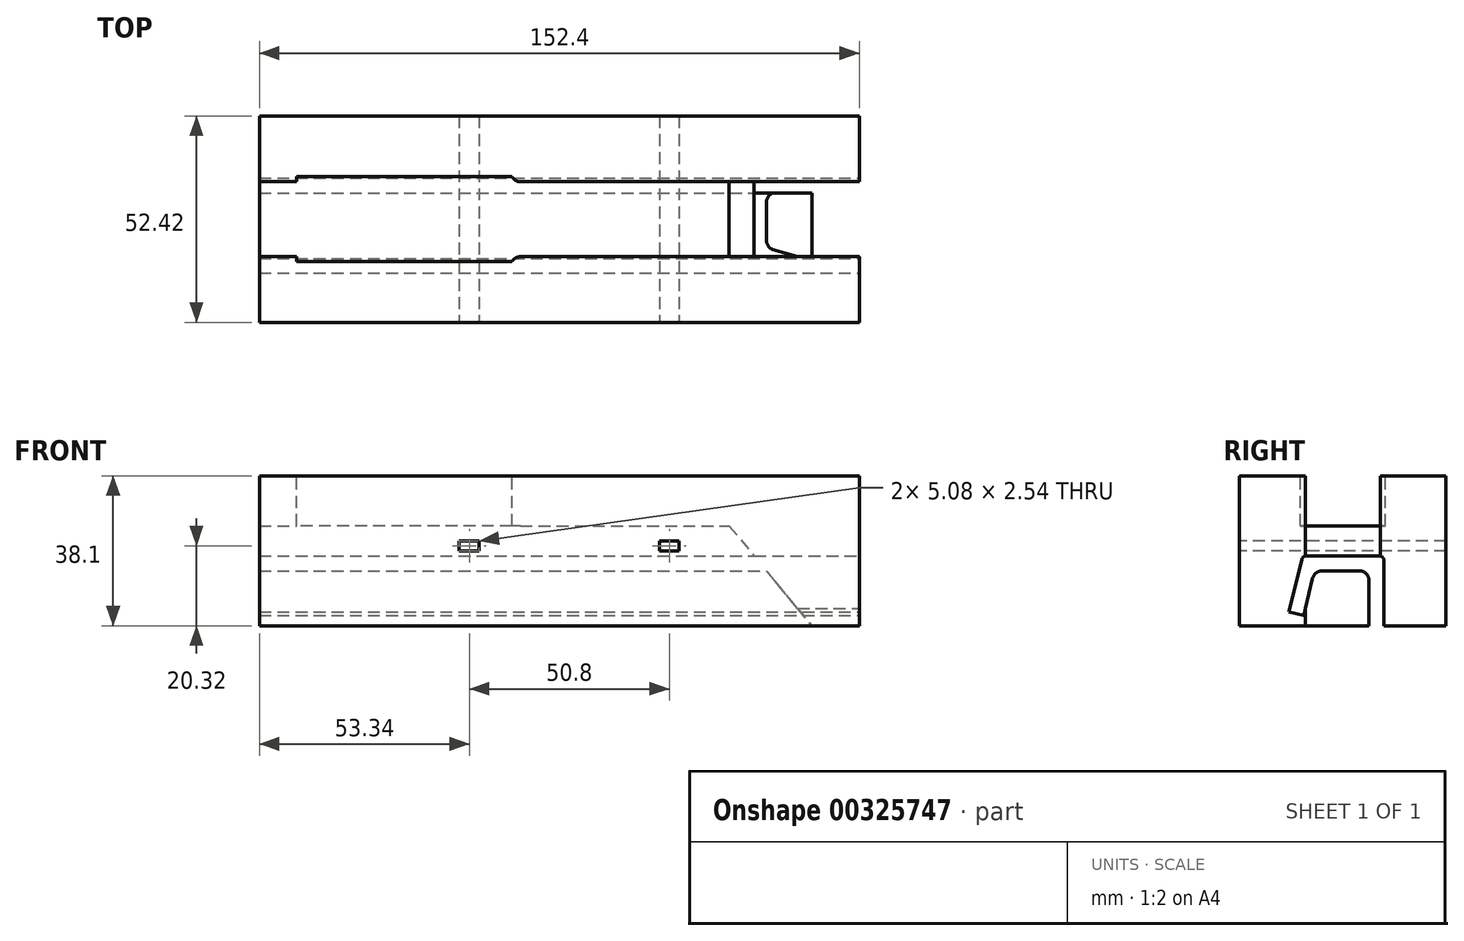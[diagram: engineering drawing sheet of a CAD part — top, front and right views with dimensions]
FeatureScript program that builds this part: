
annotation { "Feature Type Name" : "Feature", "Feature Type Description" : "" }
export const myFeature = defineFeature(function(context is Context, id is Id, definition is map)
    precondition{}
    {
        {
            var Q0;
            Q0=qCreatedBy(makeId("Right.planeOp"),FACE);
            var sketch = newSketch(context, id + "F0", { "sketchPlane" : qUnion([Q0])});
            skLineSegment(sketch, "E0.bottom", {"start": v(-26.2, 19.05) * mm, "end": v(26.2, 19.05) * mm});
            skLineSegment(sketch, "E0.top", {"start": v(-26.2, -19.05) * mm, "end": v(26.2, -19.05) * mm});
            skLineSegment(sketch, "E0.left", {"start": v(-26.2, 19.05) * mm, "end": v(-26.2, -19.05) * mm});
            skLineSegment(sketch, "E0.right", {"start": v(26.2, 19.05) * mm, "end": v(26.2, -19.05) * mm});
            skPoint(sketch, "E0.middle", {"position": v(0, 0) * mm});
            skSolve(sketch);
        }
        {
            var Q0;
            Q0=makeQuery(id+"F0.imprint","IMPRINT",FACE,{"disambiguationData":[TD([[makeQuery(id+"F0.imprint","IMPRINT",EDGE,{"derivedFrom":sQuery(id+"F0.wireOp",EDGE,"E0.bottom")}),-1.0]])]});
            extrude(context, id + "F1", {"entities" : qUnion([Q0]), "oppositeDirection" : true, "depth" : 152.4 * mm});
        }
        {
            var Q0;
            Q0=makeQuery(id+"F1.opExtrude","CAP_FACE",FACE,{"disambiguationData":[OSD([sQuery(id+"F0.wireOp",EDGE,"E0.bottom"),sQuery(id+"F0.wireOp",EDGE,"E0.top"),sQuery(id+"F0.wireOp",EDGE,"E0.left"),sQuery(id+"F0.wireOp",EDGE,"E0.right")])],"isStart":true});
            var sketch = newSketch(context, id + "F2", { "sketchPlane" : qUnion([Q0])});
            skLineSegment(sketch, "E1", {"start": v(10.49, -19.05) * mm, "end": v(10.49, -2.54) * mm});
            skLineSegment(sketch, "E2", {"start": v(9.22, -1.27) * mm, "end": v(-9.22, -1.27) * mm});
            skLineSegment(sketch, "E3", {"start": v(-10.45, -2.24) * mm, "end": v(-13.64, -15.47) * mm});
            skLineSegment(sketch, "E4", {"start": v(0, -19.05) * mm, "end": v(0, 19.05) * mm, "construction": true});
            skPoint(sketch, "E5.visualSharp", {"position": v(-10.22, -1.27) * mm});
            skArc(sketch, "E5.filletArc", {"start": v(-9.22, -1.27) * mm, "mid": v(-10, -1.54) * mm, "end": v(-10.45, -2.24) * mm});
            skPoint(sketch, "E6.visualSharp", {"position": v(10.49, -1.27) * mm});
            skArc(sketch, "E6.filletArc", {"start": v(10.49, -2.54) * mm, "mid": v(10.11, -1.64) * mm, "end": v(9.22, -1.27) * mm});
            skLineSegment(sketch, "E7", {"start": v(0, -1.27) * mm, "end": v(0, -19.05) * mm, "construction": true});
            skLineSegment(sketch, "E8.0", {"start": v(-7.22, -5.08) * mm, "end": v(-9.94, -16.36) * mm});
            skLineSegment(sketch, "E9.0", {"start": v(6.68, -5.08) * mm, "end": v(-7.22, -5.08) * mm});
            skLineSegment(sketch, "E10.0", {"start": v(6.68, -19.05) * mm, "end": v(6.68, -5.08) * mm});
            skLineSegment(sketch, "E11", {"start": v(-13.64, -15.47) * mm, "end": v(-9.94, -16.36) * mm});
            skLineSegment(sketch, "E12", {"start": v(6.68, -19.05) * mm, "end": v(10.49, -19.05) * mm});
            skSolve(sketch);
        }
        {
            var Q0;
            Q0=makeQuery(id+"F2.imprint","IMPRINT",FACE,{"disambiguationData":[TD([[makeQuery(id+"F2.imprint","IMPRINT",EDGE,{"derivedFrom":sQuery(id+"F2.wireOp",EDGE,"E1")}),1.0]])]});
            extrude(context, id + "F3", {"entities" : qUnion([Q0]), "operationType" : NewBodyOperationType.REMOVE, "endBound" : BoundingType.THROUGH_ALL, "oppositeDirection" : true, "depth" : 25.4 * mm});
        }
        {
            var Q0;
            Q0=makeQuery(id+"F1.opExtrude","SWEPT_FACE",FACE,{"disambiguationData":[OSD([sQuery(id+"F0.wireOp",EDGE,"E0.bottom")])]});
            var sketch = newSketch(context, id + "F4", { "sketchPlane" : qUnion([Q0])});
            skLineSegment(sketch, "E13.bottom", {"start": v(-88.27, -10.8) * mm, "end": v(-142.88, -10.8) * mm});
            skLineSegment(sketch, "E13.top", {"start": v(-88.27, 10.8) * mm, "end": v(-142.88, 10.8) * mm});
            skLineSegment(sketch, "E13.left", {"start": v(-88.27, -10.8) * mm, "end": v(-88.27, -9.53) * mm});
            skLineSegment(sketch, "E13.right", {"start": v(-142.88, -10.8) * mm, "end": v(-142.88, -9.53) * mm});
            skPoint(sketch, "E13.middle", {"position": v(-115.57, 0) * mm});
            skLineSegment(sketch, "E14.bottom", {"start": v(-152.4, -9.53) * mm, "end": v(-142.88, -9.53) * mm});
            skLineSegment(sketch, "E14.top", {"start": v(-152.4, 9.52) * mm, "end": v(-142.88, 9.52) * mm});
            skLineSegment(sketch, "E14.left", {"start": v(-152.4, -9.53) * mm, "end": v(-152.4, 9.52) * mm});
            skPoint(sketch, "E14.middle", {"position": v(-147.64, 0) * mm});
            skLineSegment(sketch, "E15.bottom", {"start": v(-88.27, -9.53) * mm, "end": v(0, -9.53) * mm});
            skLineSegment(sketch, "E15.top", {"start": v(-88.27, 9.53) * mm, "end": v(0, 9.53) * mm});
            skLineSegment(sketch, "E15.right", {"start": v(0, -9.53) * mm, "end": v(0, 9.53) * mm});
            skPoint(sketch, "E15.middle", {"position": v(-44.13, 0) * mm});
            skLineSegment(sketch, "E16.trimOffspring", {"start": v(-88.27, 9.53) * mm, "end": v(-88.27, 10.8) * mm});
            skLineSegment(sketch, "E17.trimOffspring", {"start": v(-142.88, 9.52) * mm, "end": v(-142.88, 10.8) * mm});
            skSolve(sketch);
        }
        {
            var Q0;
            Q0=makeQuery(id+"F4.imprint","IMPRINT",FACE,{"disambiguationData":[TD([[makeQuery(id+"F4.imprint","IMPRINT",EDGE,{"derivedFrom":sQuery(id+"F4.wireOp",EDGE,"E13.bottom")}),-1.0]])]});
            extrude(context, id + "F5", {"entities" : qUnion([Q0]), "operationType" : NewBodyOperationType.REMOVE, "oppositeDirection" : true, "depth" : 12.7 * mm});
        }
        {
            var Q0;
            Q0=makeQuery(id+"F5.boolean.opBoolean","COPY",FACE,{"derivedFrom":makeQuery(id+"F5.opExtrude","SWEPT_FACE",FACE,{"disambiguationData":[OSD([sQuery(id+"F4.wireOp",EDGE,"E15.top")])]})});
            var sketch = newSketch(context, id + "F6", { "sketchPlane" : qUnion([Q0])});
            skLineSegment(sketch, "E18", {"start": v(-33.02, 6.35) * mm, "end": v(-12.07, -19.05) * mm});
            skLineSegment(sketch, "E19", {"start": v(-12.07, -19.05) * mm, "end": v(0, -19.05) * mm});
            skLineSegment(sketch, "E20", {"start": v(0, -19.05) * mm, "end": v(0, 6.35) * mm});
            skLineSegment(sketch, "E21", {"start": v(0, 6.35) * mm, "end": v(-33.02, 6.35) * mm});
            skSolve(sketch);
        }
        {
            var Q0;
            Q0=makeQuery(id+"F6.imprint","IMPRINT",FACE,{"disambiguationData":[TD([[makeQuery(id+"F6.imprint","IMPRINT",EDGE,{"derivedFrom":sQuery(id+"F6.wireOp",EDGE,"E18")}),1.0]])]});
            var Q1;
            Q1=makeQuery(id+"F5.boolean.opBoolean","COPY",FACE,{"derivedFrom":makeQuery(id+"F5.opExtrude","SWEPT_FACE",FACE,{"disambiguationData":[OSD([sQuery(id+"F4.wireOp",EDGE,"E15.bottom")])]})});
            extrude(context, id + "F7", {"entities" : qUnion([Q0]), "operationType" : NewBodyOperationType.REMOVE, "endBound" : BoundingType.UP_TO_SURFACE, "endBoundEntityFace" : qUnion([Q1]), "depth" : 25.4 * mm});
        }
        {
            var Q0;
            Q0=makeQuery(id+"F1.opExtrude","SWEPT_FACE",FACE,{"disambiguationData":[OSD([sQuery(id+"F0.wireOp",EDGE,"E0.left")])]});
            var sketch = newSketch(context, id + "F8", { "sketchPlane" : qUnion([Q0])});
            skLineSegment(sketch, "E22.bottom", {"start": v(-96.52, 0) * mm, "end": v(-101.6, 0) * mm});
            skLineSegment(sketch, "E22.top", {"start": v(-96.52, 2.54) * mm, "end": v(-101.6, 2.54) * mm});
            skLineSegment(sketch, "E22.left", {"start": v(-96.52, 0) * mm, "end": v(-96.52, 2.54) * mm});
            skLineSegment(sketch, "E22.right", {"start": v(-101.6, 0) * mm, "end": v(-101.6, 2.54) * mm});
            skLineSegment(sketch, "E23.bottom", {"start": v(-50.8, 0) * mm, "end": v(-45.72, 0) * mm});
            skLineSegment(sketch, "E23.top", {"start": v(-50.8, 2.54) * mm, "end": v(-45.72, 2.54) * mm});
            skLineSegment(sketch, "E23.left", {"start": v(-50.8, 0) * mm, "end": v(-50.8, 2.54) * mm});
            skLineSegment(sketch, "E23.right", {"start": v(-45.72, 0) * mm, "end": v(-45.72, 2.54) * mm});
            skSolve(sketch);
        }
        {
            var Q0;
            Q0=makeQuery(id+"F8.imprint","IMPRINT",FACE,{"disambiguationData":[TD([[makeQuery(id+"F8.imprint","IMPRINT",EDGE,{"derivedFrom":sQuery(id+"F8.wireOp",EDGE,"E22.bottom")}),-1.0]])]});
            var Q1;
            Q1=makeQuery(id+"F8.imprint","IMPRINT",FACE,{"disambiguationData":[TD([[makeQuery(id+"F8.imprint","IMPRINT",EDGE,{"derivedFrom":sQuery(id+"F8.wireOp",EDGE,"E23.bottom")}),1.0]])]});
            extrude(context, id + "F9", {"entities" : qUnion([Q0, Q1]), "operationType" : NewBodyOperationType.REMOVE, "endBound" : BoundingType.THROUGH_ALL, "oppositeDirection" : true, "depth" : 25.4 * mm});
        }
        {
            var Q0;
            Q0=makeQuery(id+"F3.boolean.opBoolean","COPY",EDGE,{"derivedFrom":makeQuery(id+"F3.opExtrude","SWEPT_EDGE",EDGE,{"disambiguationData":[OSD([sQuery(id+"F2.wireOp",EDGE,"E8.0"),sQuery(id+"F2.wireOp",EDGE,"E9.0")])]})});
            var Q1;
            Q1=makeQuery(id+"F3.boolean.opBoolean","COPY",EDGE,{"derivedFrom":makeQuery(id+"F3.opExtrude","SWEPT_EDGE",EDGE,{"disambiguationData":[OSD([sQuery(id+"F2.wireOp",EDGE,"E9.0"),sQuery(id+"F2.wireOp",EDGE,"E10.0")])]})});
            fillet(context, id + "F10", {"entities" : qUnion([Q0, Q1]), "radius" : 2.54 * mm, "tangentPropagation" : true, "allowEdgeOverflow" : false});
        }
        {
            var Q0;
            Q0=makeQuery(id+"F5.boolean.opBoolean","COPY",EDGE,{"derivedFrom":makeQuery(id+"F5.opExtrude","SWEPT_EDGE",EDGE,{"disambiguationData":[OSD([sQuery(id+"F4.wireOp",EDGE,"E13.left"),sQuery(id+"F4.wireOp",EDGE,"E15.bottom")])]})});
            var Q1;
            Q1=makeQuery(id+"F5.boolean.opBoolean","COPY",EDGE,{"derivedFrom":makeQuery(id+"F5.opExtrude","SWEPT_EDGE",EDGE,{"disambiguationData":[OSD([sQuery(id+"F4.wireOp",EDGE,"E15.top"),sQuery(id+"F4.wireOp",EDGE,"E16.trimOffspring")])]})});
            fillet(context, id + "F11", {"entities" : qUnion([Q0, Q1]), "radius" : 2.54 * mm, "tangentPropagation" : true, "allowEdgeOverflow" : false});
        }
    });
